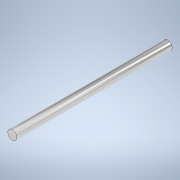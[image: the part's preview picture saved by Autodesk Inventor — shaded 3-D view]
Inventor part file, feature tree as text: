
AUTODESK INVENTOR PART (.ipt)
format: ipt  version: 2022 (Build 260153000, 153)  size: 96,768 bytes
history: native  units: mm
features: extrude x1, sketch x1
ambient origin geometry x8: Origin, YZ Plane, XZ Plane, XY Plane, X Axis, Y Axis, Z Axis, Center Point
bodies: Solid1 (feature_tree)
feature tree (2):
  extrude  "Extrusion1"  Depth=170.0mm TaperAngle=0.0deg
  sketch  "Sketch1"  dims[d0=10.0mm d1=170.0mm d2=0.0mm]
